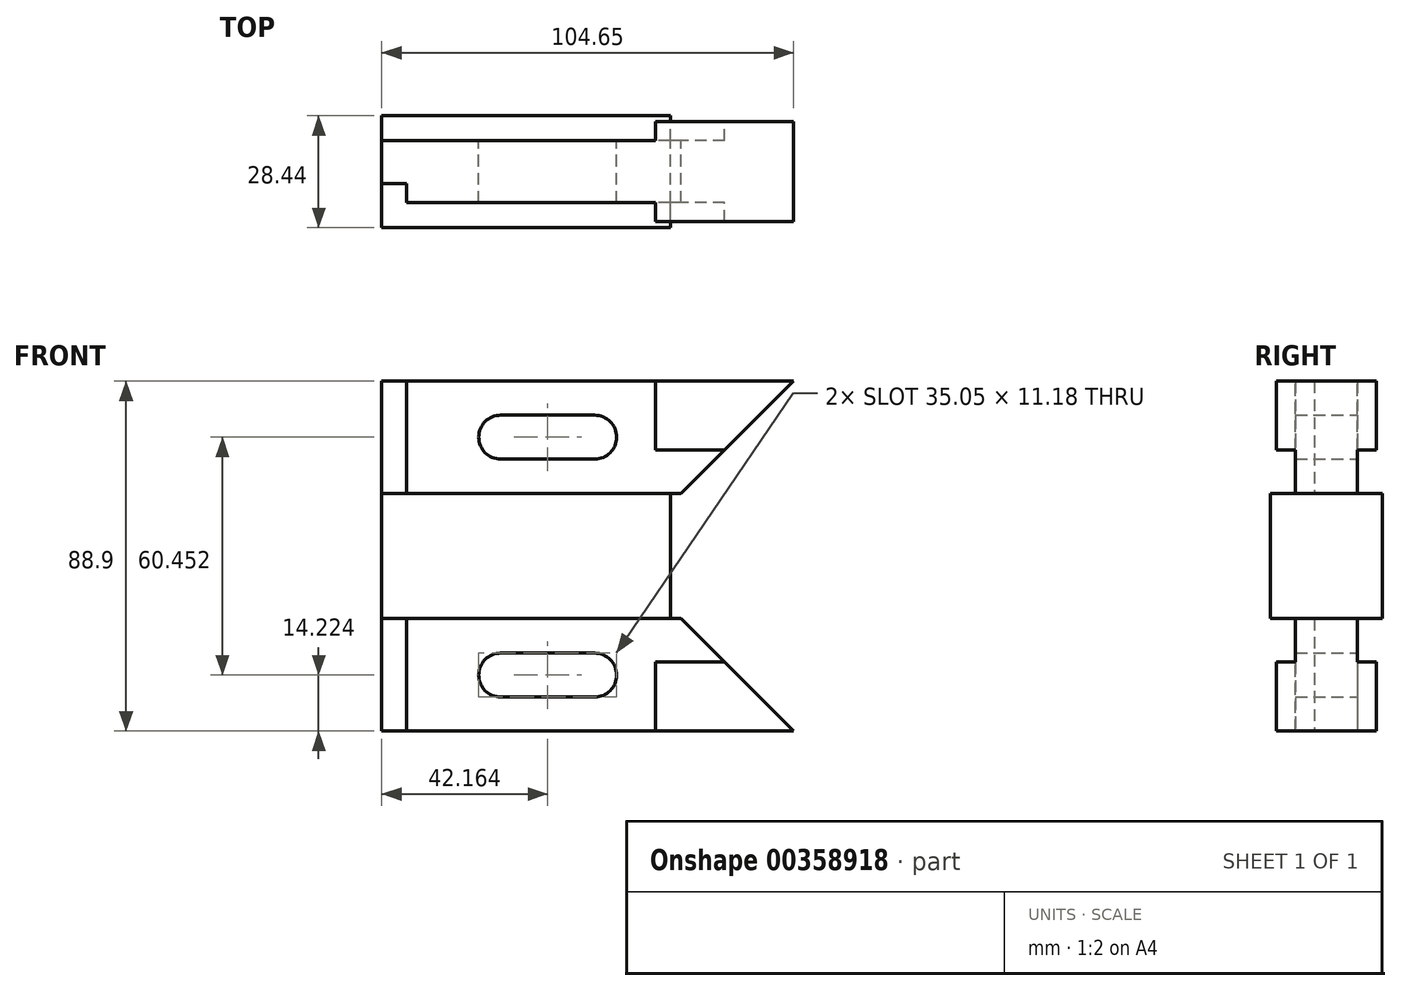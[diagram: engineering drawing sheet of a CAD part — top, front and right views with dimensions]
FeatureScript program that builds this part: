
annotation { "Feature Type Name" : "Feature", "Feature Type Description" : "" }
export const myFeature = defineFeature(function(context is Context, id is Id, definition is map)
    precondition{}
    {
        {
            var Q0;
            Q0=qCreatedBy(makeId("Front.planeOp"),FACE);
            var sketch = newSketch(context, id + "F0", { "sketchPlane" : qUnion([Q0])});
            skLineSegment(sketch, "E0", {"start": v(-93.21, 0) * mm, "end": v(145.82, 0) * mm, "construction": true});
            skLineSegment(sketch, "E1", {"start": v(0, 44.45) * mm, "end": v(104.65, 44.45) * mm});
            skLineSegment(sketch, "E2", {"start": v(104.65, 44.45) * mm, "end": v(76.07, 15.87) * mm});
            skLineSegment(sketch, "E3", {"start": v(76.07, 15.88) * mm, "end": v(0, 15.87) * mm});
            skLineSegment(sketch, "E4", {"start": v(0, 44.45) * mm, "end": v(0, -44.45) * mm});
            skPoint(sketch, "E5.orphan", {"position": v(0, 105.93) * mm});
            skLineSegment(sketch, "E6", {"start": v(73.4, 15.88) * mm, "end": v(73.4, -15.88) * mm});
            skLineSegment(sketch, "E7", {"start": v(6.35, 44.45) * mm, "end": v(6.35, 15.87) * mm});
            skLineSegment(sketch, "E8.MirrorCS", {"start": v(104.65, -44.45) * mm, "end": v(76.07, -15.87) * mm});
            skLineSegment(sketch, "E9.MirrorCS", {"start": v(0, -44.45) * mm, "end": v(104.65, -44.45) * mm});
            skLineSegment(sketch, "E10.MirrorCS", {"start": v(76.07, -15.88) * mm, "end": v(0, -15.87) * mm});
            skLineSegment(sketch, "E11.MirrorCS", {"start": v(6.35, -44.45) * mm, "end": v(6.35, -15.87) * mm});
            skArc(sketch, "E12", {"start": v(30.23, 35.81) * mm, "mid": v(24.64, 30.23) * mm, "end": v(30.23, 24.64) * mm});
            skArc(sketch, "E13", {"start": v(54.1, 24.64) * mm, "mid": v(59.7, 30.23) * mm, "end": v(54.1, 35.81) * mm});
            skLineSegment(sketch, "E14", {"start": v(30.23, 35.81) * mm, "end": v(54.1, 35.81) * mm});
            skLineSegment(sketch, "E15", {"start": v(30.23, 24.64) * mm, "end": v(54.1, 24.64) * mm});
            skLineSegment(sketch, "E16", {"start": v(24.64, 30.23) * mm, "end": v(59.7, 30.23) * mm, "construction": true});
            skLineSegment(sketch, "E17.MirrorCS", {"start": v(30.23, -35.81) * mm, "end": v(54.1, -35.81) * mm});
            skLineSegment(sketch, "E18.MirrorCS", {"start": v(30.23, -24.64) * mm, "end": v(54.1, -24.64) * mm});
            skArc(sketch, "E19.MirrorC", {"start": v(30.23, -35.81) * mm, "mid": v(24.64, -30.23) * mm, "end": v(30.23, -24.64) * mm});
            skArc(sketch, "E20.MirrorC", {"start": v(54.1, -24.64) * mm, "mid": v(59.7, -30.23) * mm, "end": v(54.1, -35.81) * mm});
            skLineSegment(sketch, "E21.MirrorCS", {"start": v(24.64, -30.23) * mm, "end": v(59.7, -30.23) * mm, "construction": true});
            skLineSegment(sketch, "E22", {"start": v(69.6, 44.45) * mm, "end": v(69.6, 26.92) * mm});
            skLineSegment(sketch, "E23.trimOffspring", {"start": v(69.6, 26.92) * mm, "end": v(87.12, 26.92) * mm});
            skLineSegment(sketch, "E24.MirrorCS", {"start": v(69.6, -26.92) * mm, "end": v(87.12, -26.92) * mm});
            skLineSegment(sketch, "E25.MirrorCS", {"start": v(69.6, -44.45) * mm, "end": v(69.6, -26.92) * mm});
            skSolve(sketch);
        }
        {
            var Q0;
            {var subQ7=sQuery(id+"F0.wireOp",EDGE,"E6");Q0=makeQuery(id+"F0.imprint","IMPRINT",FACE,{"disambiguationData":[TD([[makeQuery(id+"F0.imprint","IMPRINT",EDGE,{"derivedFrom":subQ7}),-1.0]])]});}
            extrude(context, id + "F1", {"entities" : qUnion([Q0]), "depth" : 14.22 * mm, "hasSecondDirection" : true, "secondDirectionOppositeDirection" : true, "secondDirectionDepth" : 14.22 * mm});
        }
        {
            var Q0;
            {var subQ1=sQuery(id+"F0.wireOp",EDGE,"E7");Q0=makeQuery(id+"F0.imprint","IMPRINT",FACE,{"disambiguationData":[TD([[makeQuery(id+"F0.imprint","IMPRINT",EDGE,{"derivedFrom":subQ1}),1.0]])]});}
            var Q1;
            {var subQ1=sQuery(id+"F0.wireOp",EDGE,"E11.MirrorCS");Q1=makeQuery(id+"F0.imprint","IMPRINT",FACE,{"disambiguationData":[TD([[makeQuery(id+"F0.imprint","IMPRINT",EDGE,{"derivedFrom":subQ1}),-1.0]])]});}
            var Q2;
            {var subQ3=sQuery(id+"F0.wireOp",EDGE,"E22");Q2=makeQuery(id+"F0.imprint","IMPRINT",FACE,{"disambiguationData":[TD([[makeQuery(id+"F0.imprint","IMPRINT",EDGE,{"derivedFrom":subQ3}),1.0]])]});}
            var Q3;
            {var subQ3=sQuery(id+"F0.wireOp",EDGE,"E24.MirrorCS");Q3=makeQuery(id+"F0.imprint","IMPRINT",FACE,{"disambiguationData":[TD([[makeQuery(id+"F0.imprint","IMPRINT",EDGE,{"derivedFrom":subQ3}),-1.0]])]});}
            extrude(context, id + "F2", {"entities" : qUnion([Q0, Q1, Q2, Q3]), "operationType" : NewBodyOperationType.ADD, "depth" : 7.87 * mm, "hasSecondDirection" : true, "secondDirectionOppositeDirection" : true, "secondDirectionDepth" : 7.87 * mm});
        }
        {
            var Q0;
            {var subQ3=sQuery(id+"F0.wireOp",EDGE,"E22");Q0=makeQuery(id+"F0.imprint","IMPRINT",FACE,{"disambiguationData":[TD([[makeQuery(id+"F0.imprint","IMPRINT",EDGE,{"derivedFrom":subQ3}),1.0]])]});}
            var Q1;
            {var subQ3=sQuery(id+"F0.wireOp",EDGE,"E24.MirrorCS");Q1=makeQuery(id+"F0.imprint","IMPRINT",FACE,{"disambiguationData":[TD([[makeQuery(id+"F0.imprint","IMPRINT",EDGE,{"derivedFrom":subQ3}),-1.0]])]});}
            extrude(context, id + "F3", {"entities" : qUnion([Q0, Q1]), "operationType" : NewBodyOperationType.ADD, "depth" : 12.7 * mm, "hasSecondDirection" : true, "secondDirectionOppositeDirection" : true, "secondDirectionDepth" : 12.7 * mm});
        }
        {
            var Q0;
            {var subQ3=sQuery(id+"F0.wireOp",EDGE,"E7");Q0=makeQuery(id+"F0.imprint","IMPRINT",FACE,{"disambiguationData":[TD([[makeQuery(id+"F0.imprint","IMPRINT",EDGE,{"derivedFrom":subQ3}),-1.0]])]});}
            var Q1;
            {var subQ5=sQuery(id+"F0.wireOp",EDGE,"E11.MirrorCS");Q1=makeQuery(id+"F0.imprint","IMPRINT",FACE,{"disambiguationData":[TD([[makeQuery(id+"F0.imprint","IMPRINT",EDGE,{"derivedFrom":subQ5}),1.0]])]});}
            extrude(context, id + "F4", {"entities" : qUnion([Q0, Q1]), "operationType" : NewBodyOperationType.ADD, "depth" : 3.05 * mm, "hasSecondDirection" : true, "secondDirectionOppositeDirection" : true, "secondDirectionDepth" : 7.87 * mm});
        }
    });
